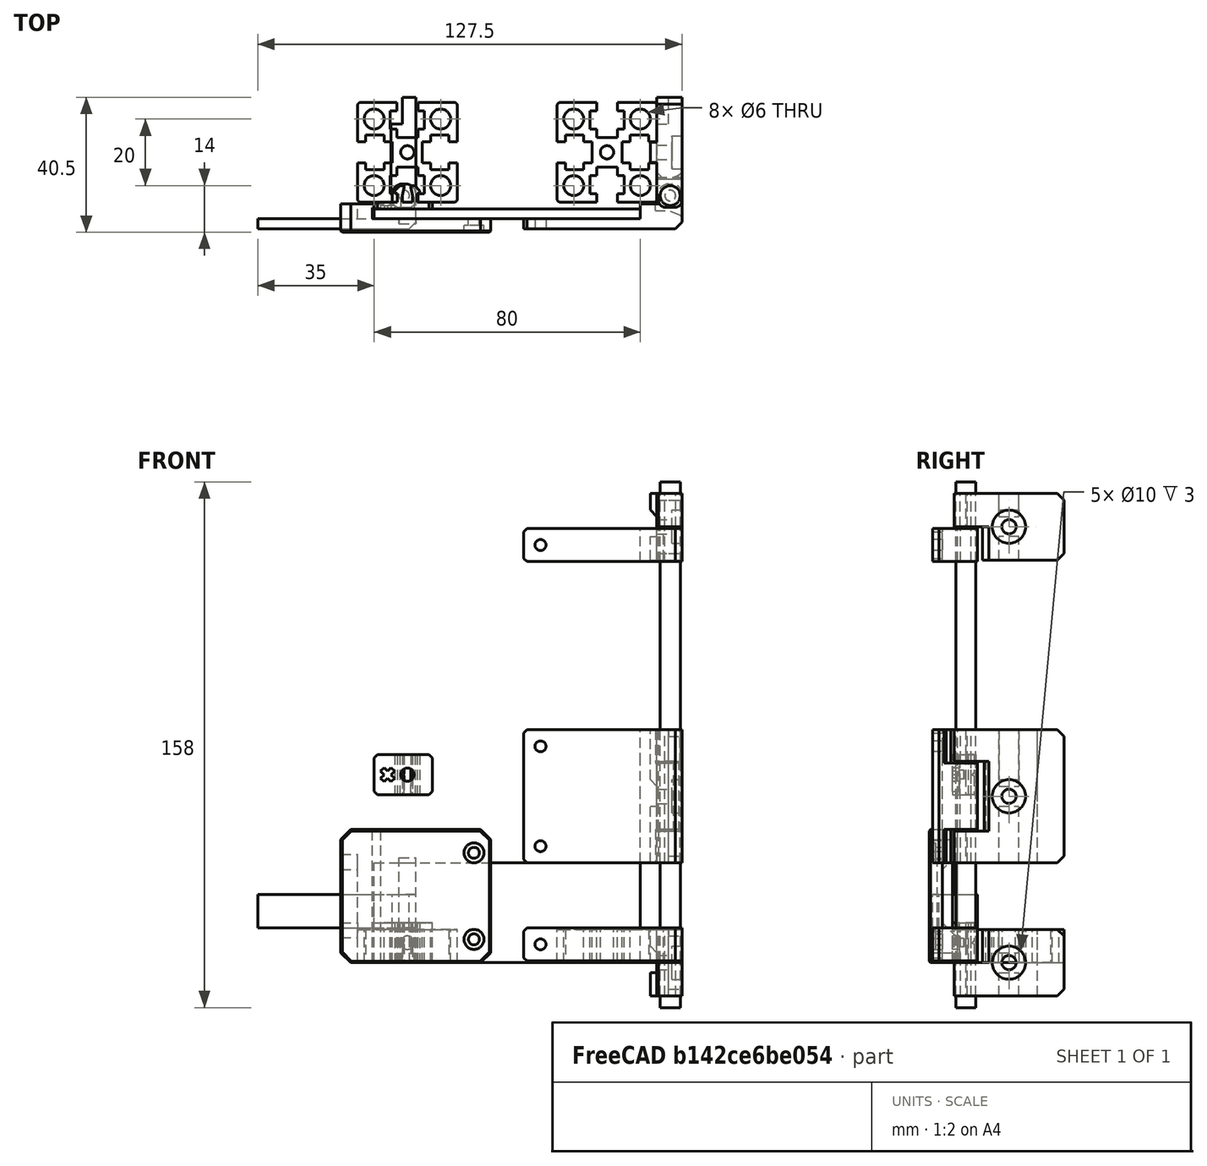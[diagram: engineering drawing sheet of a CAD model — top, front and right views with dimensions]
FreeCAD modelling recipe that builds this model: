
FCSTD DOCUMENT  (FreeCAD 0.18R16146 (Git))
Label: front-door
License: All rights reserved
LicenseURL: http://en.wikipedia.org/wiki/All_rights_reserved
objects: Part::Cut×29, Part::Chamfer×27, Part::Box×26, Part::Cylinder×23, Part::Feature×21, Part::MultiFuse×13, Part::Fillet×2
note: 141 computed .brp shape members not serialized (recipe doc carries the construction recipe); baked Part::Feature solids carry a one-line shape summary decoded from their .brp

FEATURE [Part::Box] Box001  label="Cube001"
  AttacherType = Attacher::AttachEngine3D
  Height = 10
  Length = 47.5
  Placement = pos=(-40,-8,0) rot=(0,0,1;0rad)
  Width = 3
FEATURE [Part::Feature] Cut001005004006009  label="extrusion-template001"
  Placement = pos=(65,15,0) rot=(0,0,1;0rad)
  shape: bbox 30 x 30 x 10 mm, 63 faces (baked)
FEATURE [Part::Box] Box002  label="Cube002"
  AttacherType = Attacher::AttachEngine3D
  Height = 10
  Length = 12.5
  Placement = pos=(-5,-5,0) rot=(0,0,1;0rad)
  Width = 4.5
FEATURE [Part::Cylinder] Cylinder
  Angle = 360
  AttacherType = Attacher::AttachEngine3D
  Height = 158
  Placement = pos=(84,2,-13.5) rot=(0,0,1;0rad)
  Radius = 3
FEATURE [Part::Box] Box004  label="Cube004"
  AttacherType = Attacher::AttachEngine3D
  Height = 10
  Length = 7
  Placement = pos=(0.5,-1,0) rot=(0,0,1;0rad)
  Width = 6.5
FEATURE [Part::Fillet] Fillet
  Base = -> Box004
  Edges = 2 edges r=3: [Edge3,Edge7]
FEATURE [Part::Chamfer] Chamfer
  Base = -> Box001
  Edges = 1 edges r=2: [Edge5]
FEATURE [Part::MultiFuse] Fusion  label="arm-org"
  Placement = pos=(0,0,10.5) rot=(0,0,1;0rad)
  Shapes = -> [Chamfer,Fillet,Box002]
FEATURE [Part::Cylinder] Cylinder001
  Angle = 360
  AttacherType = Attacher::AttachEngine3D
  Height = 10
  Placement = pos=(4,2,0) rot=(0,0,1;0rad)
  Radius = 1.6
FEATURE [Part::Box] Box005  label="Cube005"
  AttacherType = Attacher::AttachEngine3D
  Height = 10
  Length = 7
  Placement = pos=(0.5,-1.5,0) rot=(0,0,1;0rad)
  Width = 8.5
FEATURE [Part::Box] Box006  label="Cube006"
  AttacherType = Attacher::AttachEngine3D
  Height = 10
  Length = 7.5
  Placement = pos=(0,1.5,0) rot=(0,0,1;0rad)
  Width = 30
FEATURE [Part::Chamfer] Chamfer001
  Base = -> Box005
  Edges = 1 edges r=2.5: [Edge7]
FEATURE [Part::Fillet] Fillet001
  Base = -> Chamfer001
  Edges = 2 edges r=2: [Edge3,Edge12]
FEATURE [Part::Chamfer] Chamfer002
  Base = -> Box006
  Edges = 1 edges r=1: [Edge1]
FEATURE [Part::Box] Box007  label="Cube007"
  AttacherType = Attacher::AttachEngine3D
  Height = 10
  Length = 3.5
  Placement = pos=(0,23.5,0) rot=(0,0,1;0rad)
  Width = 8
FEATURE [Part::Cut] Cut
  Base = -> Chamfer002
  Tool = -> Box007
FEATURE [Part::MultiFuse] Fusion001  label="base-org"
  Shapes = -> [Cut,Fillet001]
FEATURE [Part::Feature] Fusion001001  label="base-org001"
  Placement = pos=(80,0,0) rot=(0,0,1;0rad)
  shape: bbox 7.5 x 33 x 10 mm, 12 faces (baked)
FEATURE [Part::Feature] Fusion001002  label="arm-org001"
  Placement = pos=(80,0,0) rot=(0,0,1;0rad)
  shape: bbox 47.5 x 13.5 x 10 mm, 13 faces (baked)
FEATURE [Part::Feature] Fusion001003  label="arm-org002"
  Placement = pos=(80,0,100) rot=(0,0,1;0rad)
  shape: bbox 47.5 x 13.5 x 10 mm, 13 faces (baked)
FEATURE [Part::Feature] Fusion001004  label="base-org002"
  Placement = pos=(80,0,121) rot=(0,0,1;0rad)
  shape: bbox 7.5 x 33 x 10 mm, 12 faces (baked)
FEATURE [Part::Feature] Fusion001005  label="base-org003"
  Placement = pos=(80,0,131) rot=(0,0,1;0rad)
  shape: bbox 7.5 x 33 x 10 mm, 12 faces (baked)
FEATURE [Part::MultiFuse] Fusion001006
  Shapes = -> [Fusion001005,Fusion001004]
FEATURE [Part::Feature] Fusion001007  label="base-org004"
  Placement = pos=(80,0,-10) rot=(0,0,1;0rad)
  shape: bbox 7.5 x 33 x 10 mm, 12 faces (baked)
FEATURE [Part::MultiFuse] Fusion001008
  Shapes = -> [Fusion001001,Fusion001007]
FEATURE [Part::Feature] Fusion001009  label="base-org005"
  Placement = pos=(80,0,30) rot=(0,0,1;0rad)
  shape: bbox 7.5 x 33 x 10 mm, 12 faces (baked)
FEATURE [Part::Feature] Fusion001010  label="arm-org003"
  Placement = pos=(80,0,29.5) rot=(0,0,1;0rad)
  shape: bbox 47.5 x 13.5 x 10 mm, 13 faces (baked)
FEATURE [Part::Feature] Fusion001011  label="arm-org004"
  Placement = pos=(80,0,39.5) rot=(0,0,1;0rad)
  shape: bbox 47.5 x 13.5 x 10 mm, 13 faces (baked)
FEATURE [Part::Feature] Fusion001012  label="base-org006"
  Placement = pos=(80,0,40) rot=(0,0,1;0rad)
  shape: bbox 7.5 x 33 x 10 mm, 12 faces (baked)
FEATURE [Part::Feature] Fusion001013  label="base-org007"
  Placement = pos=(80,0,50) rot=(0,0,1;0rad)
  shape: bbox 7.5 x 33 x 10 mm, 12 faces (baked)
FEATURE [Part::Feature] Fusion001014  label="base-org008"
  Placement = pos=(80,0,60) rot=(0,0,1;0rad)
  shape: bbox 7.5 x 33 x 10 mm, 12 faces (baked)
FEATURE [Part::MultiFuse] Fusion001016
  Shapes = -> [Fusion001009,Fusion001012,Fusion001013,Fusion001014]
FEATURE [Part::Box] Box008  label="Cube008"
  AttacherType = Attacher::AttachEngine3D
  Height = 21
  Length = 10
  Placement = pos=(79.5,-2.5,39.5) rot=(0,0,1;0rad)
  Width = 10
FEATURE [Part::Cut] Cut001005004006010
  Base = -> Fusion001016
  Tool = -> Box008
FEATURE [Part::Feature] Fusion001017  label="arm-org005"
  Placement = pos=(80,0,19.5) rot=(0,0,1;0rad)
  shape: bbox 47.5 x 13.5 x 10 mm, 13 faces (baked)
FEATURE [Part::Feature] Fusion001018  label="arm-org006"
  Placement = pos=(80,0,49.5) rot=(0,0,1;0rad)
  shape: bbox 47.5 x 13.5 x 10 mm, 13 faces (baked)
FEATURE [Part::Box] Box009  label="Cube009"
  AttacherType = Attacher::AttachEngine3D
  Height = 40
  Length = 10
  Placement = pos=(79.5,-2.5,30) rot=(0,0,1;0rad)
  Width = 10
FEATURE [Part::Box] Box010  label="Cube010"
  AttacherType = Attacher::AttachEngine3D
  Height = 40
  Length = 10
  Placement = pos=(79.5,-2.5,30) rot=(0,0,1;0rad)
  Width = 10
FEATURE [Part::Cut] Cut001005004006011
  Base = -> Fusion001018
  Tool = -> Box009
FEATURE [Part::Cut] Cut001005004006012
  Base = -> Fusion001017
  Tool = -> Box010
FEATURE [Part::Chamfer] Chamfer003
  Base = -> Cut001005004006011
  Edges = 1 edges r=2: [Edge14]
FEATURE [Part::Chamfer] Chamfer004
  Base = -> Cut001005004006012
  Edges = 1 edges r=2: [Edge14]
FEATURE [Part::Chamfer] Chamfer005
  Base = -> Chamfer003
  Edges = 1 edges r=2: [Edge14]
FEATURE [Part::Chamfer] Chamfer006
  Base = -> Chamfer004
  Edges = 1 edges r=2: [Edge14]
FEATURE [Part::MultiFuse] Fusion001019
  Shapes = -> [Chamfer006,Fusion001010,Fusion001011,Chamfer005]
FEATURE [Part::Chamfer] Chamfer007
  Base = -> Fusion001008
  Edges = 2 edges r=2: [Edge11,Edge37]
FEATURE [Part::Chamfer] Chamfer008
  Base = -> Fusion001006
  Edges = 2 edges r=2: [Edge11,Edge37]
FEATURE [Part::Chamfer] Chamfer009
  Base = -> Cut001005004006010
  Edges = 2 edges r=2: [Edge14,Edge78]
FEATURE [Part::Cylinder] Cylinder002
  Angle = 360
  AttacherType = Attacher::AttachEngine3D
  Height = 31
  Placement = pos=(75,15,1.6e-14) rot=(0,1,0;1.5708rad)
  Radius = 2.15
FEATURE [Part::Cylinder] Cylinder003
  Angle = 360
  AttacherType = Attacher::AttachEngine3D
  Height = 158
  Placement = pos=(84,2,-13.5) rot=(0,0,1;0rad)
  Radius = 1.65
FEATURE [Part::Cylinder] Cylinder004
  Angle = 360
  AttacherType = Attacher::AttachEngine3D
  Height = 158
  Placement = pos=(84,2,-13.5) rot=(0,0,1;0rad)
  Radius = 1.6
FEATURE [Part::Cylinder] Cylinder005
  Angle = 360
  AttacherType = Attacher::AttachEngine3D
  Height = 158
  Placement = pos=(84,2,-13.5) rot=(0,0,1;0rad)
  Radius = 1.65
FEATURE [Part::Cylinder] Cylinder006
  Angle = 360
  AttacherType = Attacher::AttachEngine3D
  Height = 158
  Placement = pos=(84,2,-13.5) rot=(0,0,1;0rad)
  Radius = 1.6
FEATURE [Part::Cylinder] Cylinder007
  Angle = 360
  AttacherType = Attacher::AttachEngine3D
  Height = 158
  Placement = pos=(84,2,-13.5) rot=(0,0,1;0rad)
  Radius = 1.65
FEATURE [Part::Cylinder] Cylinder008
  Angle = 360
  AttacherType = Attacher::AttachEngine3D
  Height = 158
  Placement = pos=(84,2,-13.5) rot=(0,0,1;0rad)
  Radius = 1.6
FEATURE [Part::Cut] Cut001005004006013
  Base = -> Chamfer007
  Tool = -> Cylinder008
FEATURE [Part::Cut] Cut001005004006014
  Base = -> Fusion001002
  Tool = -> Cylinder007
FEATURE [Part::Cut] Cut001005004006015
  Base = -> Chamfer009
  Tool = -> Cylinder006
FEATURE [Part::Cut] Cut001005004006016
  Base = -> Fusion001019
  Tool = -> Cylinder005
FEATURE [Part::Cut] Cut001005004006017
  Base = -> Fusion001003
  Tool = -> Cylinder004
FEATURE [Part::Cut] Cut001005004006018
  Base = -> Chamfer008
  Tool = -> Cylinder003
FEATURE [Part::Cylinder] Cylinder009
  Angle = 360
  AttacherType = Attacher::AttachEngine3D
  Height = 31
  Placement = pos=(75,15,50) rot=(0,1,0;1.5708rad)
  Radius = 2.15
FEATURE [Part::Cylinder] Cylinder010
  Angle = 360
  AttacherType = Attacher::AttachEngine3D
  Height = 31
  Placement = pos=(75,15,131) rot=(0,1,0;1.5708rad)
  Radius = 2.15
FEATURE [Part::Cylinder] Cylinder011
  Angle = 360
  AttacherType = Attacher::AttachEngine3D
  Height = 31
  Placement = pos=(84.5,15,131) rot=(0,1,0;1.5708rad)
  Radius = 5
FEATURE [Part::Cylinder] Cylinder012
  Angle = 360
  AttacherType = Attacher::AttachEngine3D
  Height = 31
  Placement = pos=(84.5,15,50) rot=(0,1,0;1.5708rad)
  Radius = 5
FEATURE [Part::Cylinder] Cylinder013
  Angle = 360
  AttacherType = Attacher::AttachEngine3D
  Height = 31
  Placement = pos=(84.5,15,1.81e-14) rot=(0,1,0;1.5708rad)
  Radius = 5
FEATURE [Part::Cut] Cut001005004006019
  Base = -> Cut001005004006018
  Tool = -> Cylinder010
FEATURE [Part::Cut] Cut001005004006020
  Base = -> Cut001005004006015
  Tool = -> Cylinder009
FEATURE [Part::Cut] Cut001005004006021
  Base = -> Cut001005004006013
  Tool = -> Cylinder002
FEATURE [Part::Cut] Cut001005004006022
  Base = -> Cut001005004006019
  Tool = -> Cylinder011
FEATURE [Part::Cut] Cut001005004006024
  Base = -> Cut001005004006020
  Tool = -> Cylinder012
FEATURE [Part::Feature] Cut001005004006024001  label="Cut001005004006025"
  shape: bbox 7.5 x 33 x 40 mm, 27 faces (baked)
FEATURE [Part::Chamfer] Chamfer010
  Base = -> Cut001005004006024001
  Edges = 1 edges r=1.5: [Edge19]
FEATURE [Part::Chamfer] Chamfer011
  Base = -> Chamfer010
  Edges = 1 edges r=1: [Edge2]
FEATURE [Part::Cut] Cut001005004006024002
  Base = -> Cut001005004006021
  Tool = -> Cylinder013
FEATURE [Part::Cylinder] Cylinder014
  Angle = 360
  AttacherType = Attacher::AttachEngine3D
  Height = 10
  Placement = pos=(45,3e-15,15.5) rot=(1,0,0;1.5708rad)
  Radius = 1.65
FEATURE [Part::Cylinder] Cylinder015
  Angle = 360
  AttacherType = Attacher::AttachEngine3D
  Height = 10
  Placement = pos=(45,7e-15,35) rot=(1,0,0;1.5708rad)
  Radius = 1.65
FEATURE [Part::Cylinder] Cylinder016
  Angle = 360
  AttacherType = Attacher::AttachEngine3D
  Height = 10
  Placement = pos=(45,1.4e-14,65) rot=(1,0,0;1.5708rad)
  Radius = 1.65
FEATURE [Part::Cylinder] Cylinder017
  Angle = 360
  AttacherType = Attacher::AttachEngine3D
  Height = 10
  Placement = pos=(45,2.52e-14,115.5) rot=(1,0,0;1.5708rad)
  Radius = 1.65
FEATURE [Part::Cut] Cut001005004006024003
  Base = -> Cut001005004006017
  Tool = -> Cylinder017
FEATURE [Part::Cut] Cut001005004006024004
  Base = -> Cut001005004006016
  Tool = -> Cylinder016
FEATURE [Part::Cut] Cut001005004006024005
  Base = -> Cut001005004006024004
  Tool = -> Cylinder015
FEATURE [Part::Cut] Cut001005004006024006
  Base = -> Cut001005004006014
  Tool = -> Cylinder014
FEATURE [Part::Chamfer] Chamfer012  label="top-hingle"
  Base = -> Cut001005004006024003
  Edges = 2 edges r=1: [Edge10,Edge26]
  Placement = pos=(0,0,10) rot=(0,0,1;0rad)
FEATURE [Part::Chamfer] Chamfer013  label="mid-gingle"
  Base = -> Cut001005004006024005
  Edges = 2 edges r=1: [Edge9,Edge107]
FEATURE [Part::Chamfer] Chamfer014  label="btm-hingle"
  Base = -> Cut001005004006024006
  Edges = 2 edges r=1: [Edge10,Edge26]
  Placement = pos=(0,0,-10) rot=(0,0,1;0rad)
FEATURE [Part::Box] Box011  label="Cube011"
  AttacherType = Attacher::AttachEngine3D
  Height = 7
  Length = 3
  Placement = pos=(78,12,-10) rot=(0,0,1;0rad)
  Width = 6
FEATURE [Part::Box] Box012  label="Cube012"
  AttacherType = Attacher::AttachEngine3D
  Height = 7
  Length = 3
  Placement = pos=(78,12,3) rot=(0,0,1;0rad)
  Width = 6
FEATURE [Part::Box] Box013  label="Cube013"
  AttacherType = Attacher::AttachEngine3D
  Height = 17
  Length = 3
  Placement = pos=(78,12,30) rot=(0,0,1;0rad)
  Width = 6
FEATURE [Part::Box] Box014  label="Cube014"
  AttacherType = Attacher::AttachEngine3D
  Height = 17
  Length = 3
  Placement = pos=(78,12,53) rot=(0,0,1;0rad)
  Width = 6
FEATURE [Part::Box] Box015  label="Cube015"
  AttacherType = Attacher::AttachEngine3D
  Height = 7
  Length = 3
  Placement = pos=(78,12,121) rot=(0,0,1;0rad)
  Width = 6
FEATURE [Part::Box] Box016  label="Cube016"
  AttacherType = Attacher::AttachEngine3D
  Height = 7
  Length = 3
  Placement = pos=(78,12,134) rot=(0,0,1;0rad)
  Width = 6
FEATURE [Part::Chamfer] Chamfer015
  Base = -> Box016
  Edges = 1 edges r=2: [Edge4]
FEATURE [Part::Chamfer] Chamfer016
  Base = -> Box014
  Edges = 1 edges r=2: [Edge4]
FEATURE [Part::Chamfer] Chamfer017
  Base = -> Box012
  Edges = 1 edges r=2: [Edge4]
FEATURE [Part::Box] Box017  label="Cube017"
  AttacherType = Attacher::AttachEngine3D
  Height = 20
  Length = 4
  Placement = pos=(80,23,121) rot=(0,0,1;0rad)
  Width = 8.5
FEATURE [Part::Chamfer] Chamfer018
  Base = -> Box017
  Edges = 2 edges r=2: [Edge11,Edge12]
FEATURE [Part::MultiFuse] Fusion001020  label="top-base"
  Shapes = -> [Chamfer018,Cut001005004006022,Chamfer015,Box015]
FEATURE [Part::MultiFuse] Fusion001021  label="mid-base"
  Shapes = -> [Chamfer011,Chamfer016,Box013]
FEATURE [Part::MultiFuse] Fusion001022  label="btm-base"
  Shapes = -> [Cut001005004006024002,Chamfer017,Box011]
FEATURE [Part::Feature] Cut001005004006024007  label="extrusion-template002"
  Placement = pos=(5,15,0) rot=(0,0,1;0rad)
  shape: bbox 30 x 30 x 10 mm, 63 faces (baked)
FEATURE [Part::Box] Box018  label="acrylic-pref-1"
  AttacherType = Attacher::AttachEngine3D
  Height = 30
  Length = 80
  Placement = pos=(-5,-5,0) rot=(0,0,1;0rad)
  Width = 3
FEATURE [Part::Box] Box  label="Cube"
  AttacherType = Attacher::AttachEngine3D
  Height = 19.5
  Length = 5
  Placement = pos=(2.5,-6.5,10.5) rot=(0,0,1;0rad)
  Width = 1.5
FEATURE [Part::Box] Box019  label="Cube018"
  AttacherType = Attacher::AttachEngine3D
  Height = 40
  Length = 45
  Placement = pos=(-15,-9,0) rot=(0,0,1;0rad)
  Width = 4
FEATURE [Part::Box] Box020  label="Cube019"
  AttacherType = Attacher::AttachEngine3D
  Height = 40
  Length = 9.5
  Placement = pos=(-15,-5,0) rot=(0,0,1;0rad)
  Width = 4.5
FEATURE [Part::Box] Box021  label="Cube020"
  AttacherType = Attacher::AttachEngine3D
  Height = 40
  Length = 7
  Placement = pos=(-10,-1.7,0) rot=(0,0,1;0rad)
  Width = 1.2
FEATURE [Part::Cut] Cut001005004006024008
  Base = -> Box019
  Tool = -> Box
FEATURE [Part::Chamfer] Chamfer019
  Base = -> Cut001005004006024008
  Edges = 1 edges r=1.49: [Edge12]
FEATURE [Part::Chamfer] Chamfer020
  Base = -> Chamfer019
  Edges = 2 edges r=3: [Edge22,Edge25]
FEATURE [Part::Cylinder] Cylinder018
  Angle = 360
  AttacherType = Attacher::AttachEngine3D
  Height = 10
  Placement = pos=(25,-9,7) rot=(1,0,0;4.71239rad)
  Radius = 1.65
FEATURE [Part::Cylinder] Cylinder019
  Angle = 360
  AttacherType = Attacher::AttachEngine3D
  Height = 10
  Placement = pos=(25,-9,33) rot=(-1,0,0;1.5708rad)
  Radius = 1.65
FEATURE [Part::Cylinder] Cylinder020
  Angle = 360
  AttacherType = Attacher::AttachEngine3D
  Height = 2
  Placement = pos=(25,-9,33) rot=(-1,0,0;1.5708rad)
  Radius = 3
FEATURE [Part::Cylinder] Cylinder021
  Angle = 360
  AttacherType = Attacher::AttachEngine3D
  Height = 2
  Placement = pos=(25,-9,7) rot=(-1,0,0;1.5708rad)
  Radius = 3
FEATURE [Part::MultiFuse] Fusion001024
  Shapes = -> [Cylinder019,Cylinder018]
FEATURE [Part::Box] Box022  label="Cube021"
  AttacherType = Attacher::AttachEngine3D
  Height = 10
  Length = 10
  Placement = pos=(80,-3,121) rot=(0,0,1;0rad)
  Width = 10
FEATURE [Part::Box] Box023  label="Cube022"
  AttacherType = Attacher::AttachEngine3D
  Height = 10
  Length = 10
  Placement = pos=(80,-3,0) rot=(0,0,1;0rad)
  Width = 10
FEATURE [Part::Cut] Cut001005004006024012
  Base = -> Fusion001022
  Tool = -> Box023
FEATURE [Part::Cut] Cut001005004006024013
  Base = -> Fusion001020
  Tool = -> Box022
FEATURE [Part::Chamfer] Chamfer023
  Base = -> Cut001005004006024013
  Edges = 2 edges r=2: [Edge20,Edge43]
FEATURE [Part::Feature] Cut001005004006024012001  label="Cut001005004006024014"
  shape: bbox 9.5 x 33 x 20 mm, 28 faces (baked)
FEATURE [Part::Chamfer] Chamfer024
  Base = -> Cut001005004006024012001
  Edges = 2 edges r=2: [Edge38,Edge40]
FEATURE [Part::MultiFuse] Fusion001025
  Shapes = -> [Chamfer020,Box020,Box021]
FEATURE [Part::Chamfer] Chamfer025
  Base = -> Fusion001025
  Edges = 4 edges r=3: [Edge2,Edge4,Edge6,Edge7]
FEATURE [Part::Cut] Cut001005004006024012002
  Base = -> Chamfer025
  Tool = -> Fusion001024
FEATURE [Part::MultiFuse] Fusion001026
  Shapes = -> [Cylinder020,Cylinder021]
FEATURE [Part::Cut] Cut001005004006024012003
  Base = -> Cut001005004006024012002
  Tool = -> Fusion001026
FEATURE [Part::Box] Box024  label="Cube023"
  AttacherType = Attacher::AttachEngine3D
  Height = 26
  Length = 10
  Placement = pos=(-20,-5,7) rot=(0,0,1;0rad)
  Width = 10
FEATURE [Part::Chamfer] Chamfer026
  Base = -> Box024
  Edges = 2 edges r=5: [Edge9,Edge10]
FEATURE [Part::Cut] Cut001005004006024012004
  Base = -> Cut001005004006024012003
  Tool = -> Chamfer026
FEATURE [Part::Chamfer] Chamfer027
  Base = -> Cut001005004006024012004
  Edges = 8 edges r=0.4: [Edge5,Edge18,Edge19,Edge20,Edge21,Edge22,Edge23,Edge24]
FEATURE [Part::Feature] Fusion012001  label="Fusion055007"
  Placement = pos=(5,0,0) rot=(0,0,1;0rad)
  shape: bbox 25 x 11 x 12 mm, 139 faces (baked)
FEATURE [Part::Box] Box025  label="Cube024"
  AttacherType = Attacher::AttachEngine3D
  Height = 13
  Length = 26
  Placement = pos=(-8,-12,0) rot=(0,0,1;0rad)
  Width = 10
FEATURE [Part::Cut] Cut001005004006024012005
  Base = -> Fusion012001
  Tool = -> Box025
FEATURE [Part::Cylinder] Cylinder022
  Angle = 360
  AttacherType = Attacher::AttachEngine3D
  Height = 10
  Placement = pos=(5,1.5,6) rot=(1,0,0;1.5708rad)
  Radius = 2
FEATURE [Part::Box] Box026  label="Cube025"
  AttacherType = Attacher::AttachEngine3D
  Height = 12
  Length = 17.5
  Placement = pos=(-5,-2,0) rot=(0,0,1;0rad)
  Width = 2
FEATURE [Part::MultiFuse] Fusion012002
  Shapes = -> [Cut001005004006024012005,Box026]
FEATURE [Part::Cut] Cut001005004006024012006
  Base = -> Fusion012002
  Tool = -> Cylinder022
FEATURE [Part::Feature] Fusion012003001001  label="Fusion055009"
  Placement = pos=(-10.5,-1,13.75) rot=(0,0,1;0rad)
  shape: bbox 4.243 x 1 x 4.243 mm, 14 faces (baked)
FEATURE [Part::Feature] Cut001005004006024012006001  label="Cut001005004006024012007"
  shape: bbox 17.5 x 7 x 12 mm, 46 faces (baked)
FEATURE [Part::Chamfer] Chamfer028
  Base = -> Cut001005004006024012006001
  Edges = 4 edges r=1: [Edge2,Edge4,Edge57,Edge105]
FEATURE [Part::Cut] Cut001005004006024012006002
  Base = -> Chamfer028
  Placement = pos=(0,0,50.5) rot=(0,0,1;0rad)
  Tool = -> Fusion012003001001
